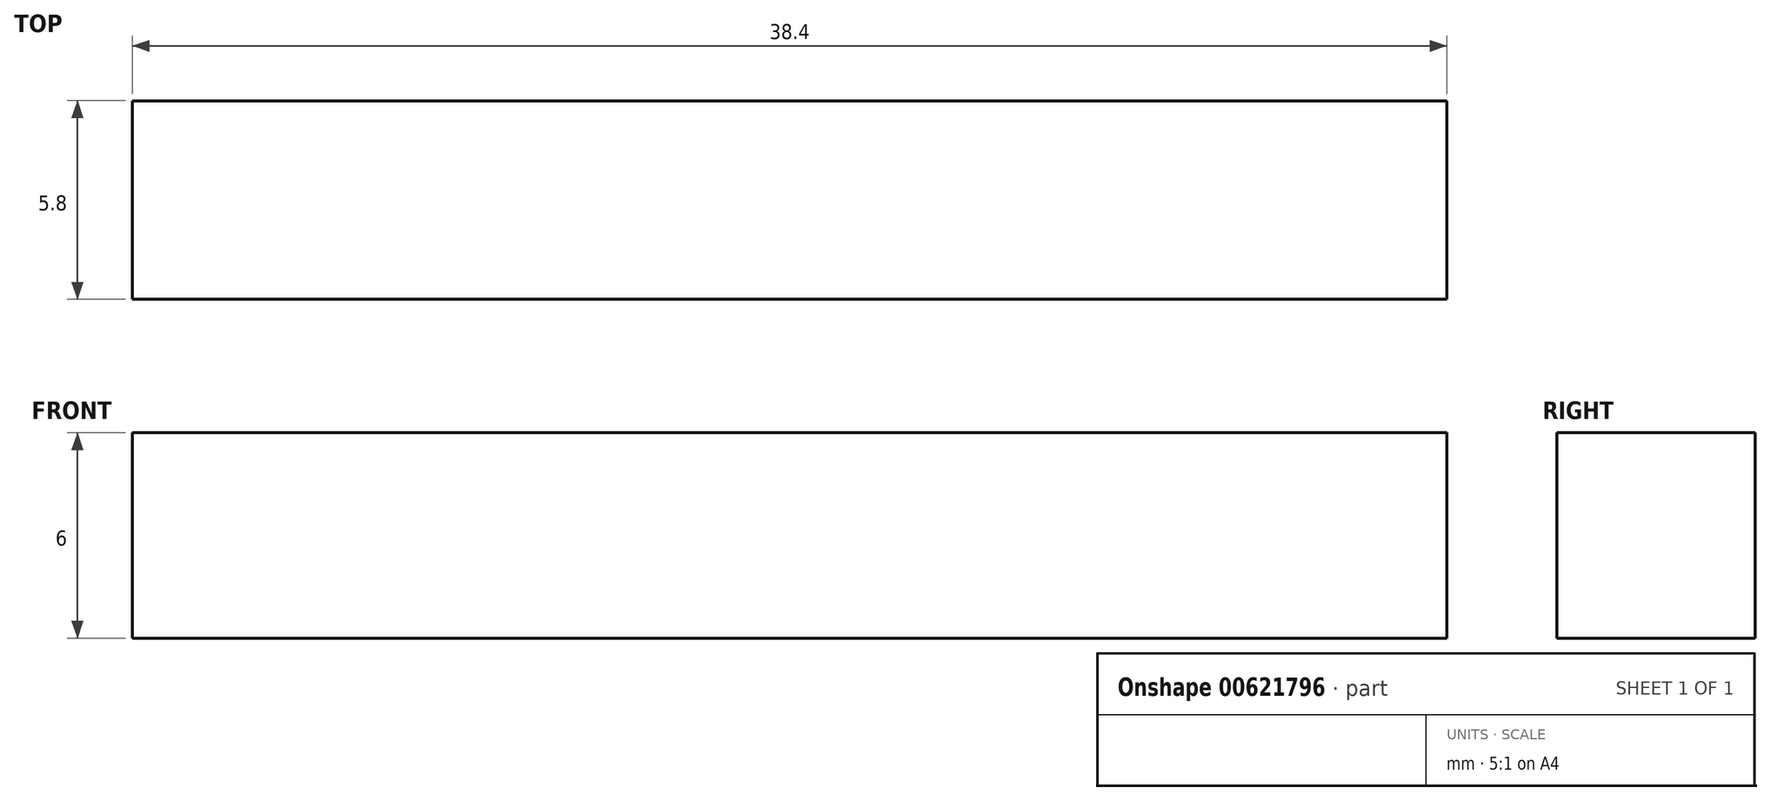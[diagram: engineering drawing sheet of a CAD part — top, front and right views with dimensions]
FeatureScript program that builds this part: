
annotation { "Feature Type Name" : "Feature", "Feature Type Description" : "" }
export const myFeature = defineFeature(function(context is Context, id is Id, definition is map)
    precondition{}
    {
        {
            var Q0;
            Q0=qCreatedBy(makeId("Top.planeOp"),FACE);
            var sketch = newSketch(context, id + "F0", { "sketchPlane" : qUnion([Q0])});
            skLineSegment(sketch, "E0.bottom", {"start": v(-19.2, 2.9) * mm, "end": v(19.2, 2.9) * mm});
            skLineSegment(sketch, "E0.top", {"start": v(-19.2, -2.9) * mm, "end": v(19.2, -2.9) * mm});
            skLineSegment(sketch, "E0.left", {"start": v(-19.2, 2.9) * mm, "end": v(-19.2, -2.9) * mm});
            skLineSegment(sketch, "E0.right", {"start": v(19.2, 2.9) * mm, "end": v(19.2, -2.9) * mm});
            skPoint(sketch, "E0.middle", {"position": v(0, 0) * mm});
            skSolve(sketch);
        }
        {
            var Q0;
            Q0=makeQuery(id+"F0.imprint","IMPRINT",FACE,{"disambiguationData":[TD([[makeQuery(id+"F0.imprint","IMPRINT",EDGE,{"derivedFrom":sQuery(id+"F0.wireOp",EDGE,"E0.bottom")}),-1.0]])]});
            extrude(context, id + "F1", {"entities" : qUnion([Q0]), "oppositeDirection" : true, "depth" : 6 * mm, "offsetDistance" : 25 * mm});
        }
    });
